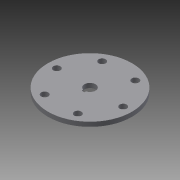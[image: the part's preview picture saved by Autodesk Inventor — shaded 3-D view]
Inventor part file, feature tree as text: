
AUTODESK INVENTOR PART (.ipt)
format: ipt  version: 2013 (Build 170138000, 138)  size: 98,816 bytes
history: native  units: in
note: dims shown in document units (in); Inventor stores cm internally (conversion verified against a paired STEP export)
features: extrude x1, sketch x1
ambient origin geometry x8: Origin, YZ Plane, XZ Plane, XY Plane, X Axis, Y Axis, Z Axis, Center Point
feature tree (2):
  extrude  "Extrusion2"  Depth=0.2in
  sketch  "Sketch1"  dims[d0=0.2in d6=0.2in d8=0.2in d10=0.2in d11=2.375in d15=0.315in d19=0.0394in d20=0.0394in d22=0.0in d23=0.0394in d24=0.125in d25=0.0in]
